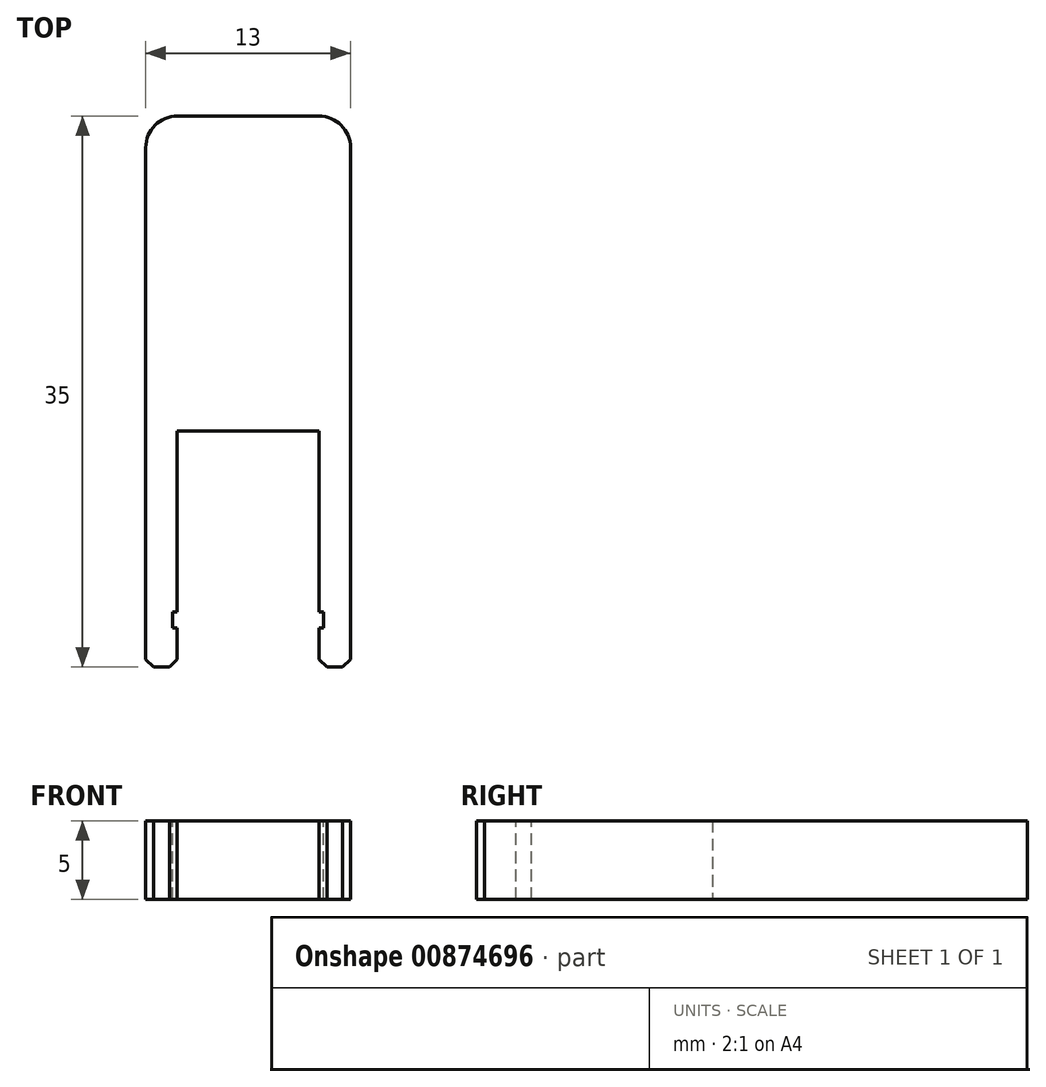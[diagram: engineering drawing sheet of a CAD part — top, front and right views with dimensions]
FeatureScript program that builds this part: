
annotation { "Feature Type Name" : "Feature", "Feature Type Description" : "" }
export const myFeature = defineFeature(function(context is Context, id is Id, definition is map)
    precondition{}
    {
        {
            var Q0;
            Q0=qCreatedBy(makeId("Top.planeOp"),FACE);
            var sketch = newSketch(context, id + "F0", { "sketchPlane" : qUnion([Q0])});
            skLineSegment(sketch, "E0", {"start": v(-6.8, 24.3) * mm, "end": v(6.2, 24.3) * mm});
            skLineSegment(sketch, "E1", {"start": v(-6.8, 24.3) * mm, "end": v(-6.8, 4.3) * mm});
            skLineSegment(sketch, "E2", {"start": v(6.2, 24.3) * mm, "end": v(6.2, 4.3) * mm});
            skLineSegment(sketch, "E3", {"start": v(-6.8, 4.3) * mm, "end": v(6.2, 4.3) * mm});
            skLineSegment(sketch, "E4", {"start": v(-6.8, 4.3) * mm, "end": v(-6.8, -10.7) * mm});
            skLineSegment(sketch, "E5", {"start": v(6.2, 4.3) * mm, "end": v(6.2, -10.7) * mm});
            skLineSegment(sketch, "E6", {"start": v(-6.8, -10.7) * mm, "end": v(-4.8, -10.7) * mm});
            skLineSegment(sketch, "E7", {"start": v(6.2, -10.7) * mm, "end": v(4.2, -10.7) * mm});
            skLineSegment(sketch, "E8", {"start": v(-4.8, -10.7) * mm, "end": v(-4.8, 4.3) * mm});
            skLineSegment(sketch, "E9", {"start": v(4.2, -10.7) * mm, "end": v(4.2, 4.3) * mm});
            skSolve(sketch);
        }
        {
            var Q0;
            Q0 = qSketchRegion(id + "F0", true);
            extrude(context, id + "F1", {"entities" : qUnion([Q0]), "depth" : 5 * mm, "offsetDistance" : 25 * mm});
        }
        {
            var Q0;
            Q0=makeQuery(id+"F1.opExtrude","SWEPT_EDGE",EDGE,{"disambiguationData":[OSD([sQuery(id+"F0.wireOp",EDGE,"E4"),sQuery(id+"F0.wireOp",EDGE,"E6")])]});
            var Q1;
            Q1=makeQuery(id+"F1.opExtrude","SWEPT_EDGE",EDGE,{"disambiguationData":[OSD([sQuery(id+"F0.wireOp",EDGE,"E7"),sQuery(id+"F0.wireOp",EDGE,"E9")])]});
            var Q2;
            Q2=makeQuery(id+"F1.opExtrude","SWEPT_EDGE",EDGE,{"disambiguationData":[OSD([sQuery(id+"F0.wireOp",EDGE,"E5"),sQuery(id+"F0.wireOp",EDGE,"E7")])]});
            var Q3;
            Q3=makeQuery(id+"F1.opExtrude","SWEPT_EDGE",EDGE,{"disambiguationData":[OSD([sQuery(id+"F0.wireOp",EDGE,"E6"),sQuery(id+"F0.wireOp",EDGE,"E8")])]});
            chamfer(context, id + "F2", {"entities" : qUnion([Q0, Q1, Q2, Q3]), "width" : 0.5 * mm, "tangentPropagation" : true});
        }
        {
            var Q0;
            Q0=makeQuery(id+"F1.opExtrude","CAP_FACE",FACE,{"disambiguationData":[OSD([sQuery(id+"F0.wireOp",EDGE,"E0"),sQuery(id+"F0.wireOp",EDGE,"E1"),sQuery(id+"F0.wireOp",EDGE,"E2"),sQuery(id+"F0.wireOp",EDGE,"E3"),sQuery(id+"F0.wireOp",EDGE,"E4"),sQuery(id+"F0.wireOp",EDGE,"E5"),sQuery(id+"F0.wireOp",EDGE,"E6"),sQuery(id+"F0.wireOp",EDGE,"E7"),sQuery(id+"F0.wireOp",EDGE,"E8"),sQuery(id+"F0.wireOp",EDGE,"E9")])],"isStart":false});
            var sketch = newSketch(context, id + "F3", { "sketchPlane" : qUnion([Q0])});
            skLineSegment(sketch, "E10.bottom", {"start": v(-4.8, -8.2) * mm, "end": v(-5.1, -8.2) * mm});
            skLineSegment(sketch, "E10.top", {"start": v(-4.8, -7.2) * mm, "end": v(-5.1, -7.2) * mm});
            skLineSegment(sketch, "E10.left", {"start": v(-4.8, -8.2) * mm, "end": v(-4.8, -7.2) * mm});
            skLineSegment(sketch, "E10.right", {"start": v(-5.1, -8.2) * mm, "end": v(-5.1, -7.2) * mm});
            skLineSegment(sketch, "E11.bottom", {"start": v(4.2, -8.2) * mm, "end": v(4.5, -8.2) * mm});
            skLineSegment(sketch, "E11.top", {"start": v(4.2, -7.2) * mm, "end": v(4.5, -7.2) * mm});
            skLineSegment(sketch, "E11.left", {"start": v(4.2, -8.2) * mm, "end": v(4.2, -7.2) * mm});
            skLineSegment(sketch, "E11.right", {"start": v(4.5, -8.2) * mm, "end": v(4.5, -7.2) * mm});
            skSolve(sketch);
        }
        {
            var Q0;
            Q0 = qSketchRegion(id + "F3", true);
            extrude(context, id + "F4", {"entities" : qUnion([Q0]), "operationType" : NewBodyOperationType.REMOVE, "oppositeDirection" : true, "depth" : 25 * mm, "offsetDistance" : 25 * mm});
        }
        {
            var Q0;
            Q0=makeQuery(id+"F1.opExtrude","SWEPT_EDGE",EDGE,{"disambiguationData":[OSD([sQuery(id+"F0.wireOp",EDGE,"E0"),sQuery(id+"F0.wireOp",EDGE,"E2")])]});
            var Q1;
            Q1=makeQuery(id+"F1.opExtrude","SWEPT_EDGE",EDGE,{"disambiguationData":[OSD([sQuery(id+"F0.wireOp",EDGE,"E0"),sQuery(id+"F0.wireOp",EDGE,"E1")])]});
            fillet(context, id + "F5", {"entities" : qUnion([Q0, Q1]), "radius" : 2 * mm, "tangentPropagation" : true, "allowEdgeOverflow" : false});
        }
    });
